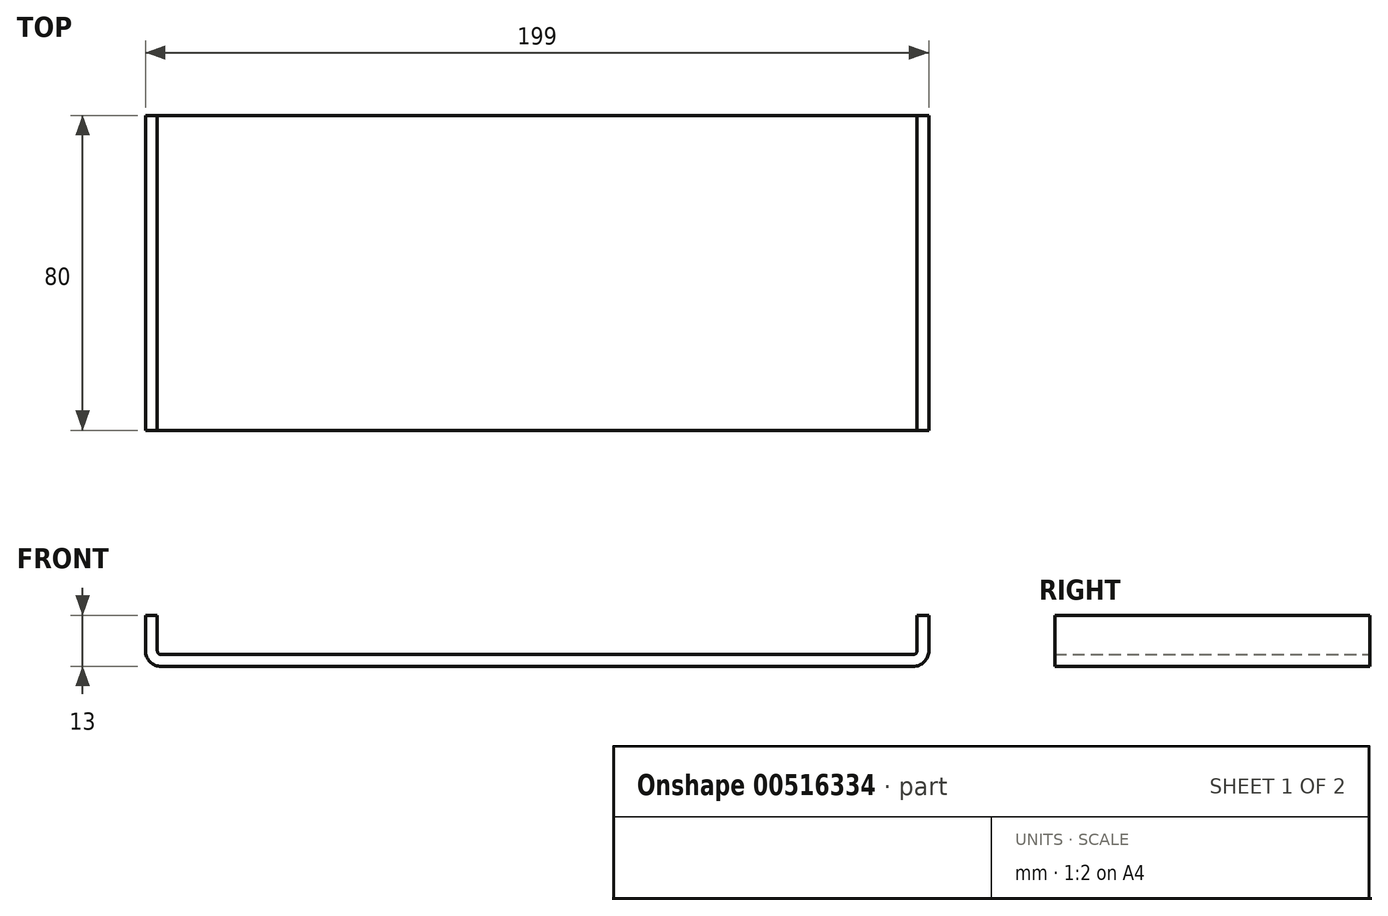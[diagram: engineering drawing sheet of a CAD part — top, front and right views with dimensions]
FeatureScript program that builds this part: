
annotation { "Feature Type Name" : "Feature", "Feature Type Description" : "" }
export const myFeature = defineFeature(function(context is Context, id is Id, definition is map)
    precondition{}
    {
        {
            var Q0;
            Q0=qCreatedBy(makeId("Front.planeOp"),FACE);
            var sketch = newSketch(context, id + "F0", { "sketchPlane" : qUnion([Q0])});
            skLineSegment(sketch, "E0.top", {"start": v(-99.5, -13) * mm, "end": v(99.5, -13) * mm});
            skLineSegment(sketch, "E0.left", {"start": v(-99.5, 0) * mm, "end": v(-99.5, -13) * mm});
            skLineSegment(sketch, "E0.right", {"start": v(99.5, 0) * mm, "end": v(99.5, -13) * mm});
            skPoint(sketch, "E0.middle", {"position": v(0, 0) * mm});
            skLineSegment(sketch, "E1", {"start": v(-99.5, 0) * mm, "end": v(-96.5, 0) * mm});
            skPoint(sketch, "E2.top.end.orphan", {"position": v(-93.5, 13) * mm});
            skPoint(sketch, "E0.bottom.start.orphan", {"position": v(-99.5, 13) * mm});
            skPoint(sketch, "E3.orphan", {"position": v(99.5, 13) * mm});
            skLineSegment(sketch, "E4.trimOffspring", {"start": v(96.5, 0) * mm, "end": v(99.5, 0) * mm});
            skLineSegment(sketch, "E5.bottom", {"start": v(96.5, 0) * mm, "end": v(96.5, 0) * mm});
            skLineSegment(sketch, "E5.top", {"start": v(-96.5, -10) * mm, "end": v(96.5, -10) * mm});
            skLineSegment(sketch, "E5.left", {"start": v(-96.5, 0) * mm, "end": v(-96.5, -10) * mm});
            skLineSegment(sketch, "E5.right", {"start": v(96.5, 0) * mm, "end": v(96.5, -10) * mm});
            skSolve(sketch);
        }
        {
            var Q0;
            Q0=makeQuery(id+"F0.imprint","IMPRINT",FACE,{"disambiguationData":[TD([[makeQuery(id+"F0.imprint","IMPRINT",EDGE,{"derivedFrom":sQuery(id+"F0.wireOp",EDGE,"E0.top")}),1.0]])]});
            extrude(context, id + "F1", {"entities" : qUnion([Q0]), "endBound" : BoundingType.SYMMETRIC, "depth" : 80 * mm, "offsetDistance" : 25 * mm});
        }
        {
            var Q0;
            Q0=makeQuery(id+"F1.opExtrude","SWEPT_EDGE",EDGE,{"disambiguationData":[OSD([sQuery(id+"F0.wireOp",EDGE,"E5.top"),sQuery(id+"F0.wireOp",EDGE,"E5.left")])]});
            var Q1;
            Q1=makeQuery(id+"F1.opExtrude","SWEPT_EDGE",EDGE,{"disambiguationData":[OSD([sQuery(id+"F0.wireOp",EDGE,"E5.top"),sQuery(id+"F0.wireOp",EDGE,"E5.right")])]});
            fillet(context, id + "F2", {"entities" : qUnion([Q0, Q1]), "radius" : 1 * mm, "tangentPropagation" : true, "allowEdgeOverflow" : false});
        }
        {
            var Q0;
            Q0=makeQuery(id+"F1.opExtrude","SWEPT_EDGE",EDGE,{"disambiguationData":[OSD([sQuery(id+"F0.wireOp",EDGE,"E0.top"),sQuery(id+"F0.wireOp",EDGE,"E0.left")])]});
            var Q1;
            Q1=makeQuery(id+"F1.opExtrude","SWEPT_EDGE",EDGE,{"disambiguationData":[OSD([sQuery(id+"F0.wireOp",EDGE,"E0.top"),sQuery(id+"F0.wireOp",EDGE,"E0.right")])]});
            fillet(context, id + "F3", {"entities" : qUnion([Q0, Q1]), "radius" : 4 * mm, "tangentPropagation" : true, "allowEdgeOverflow" : false});
        }
    });
